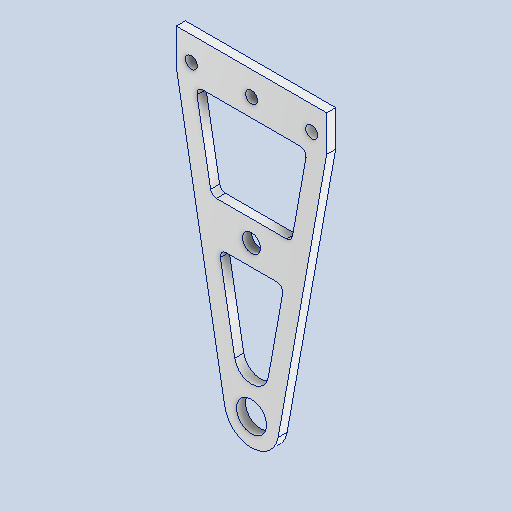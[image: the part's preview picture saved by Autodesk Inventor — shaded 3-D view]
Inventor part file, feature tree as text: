
AUTODESK INVENTOR PART (.ipt)
format: ipt  version: 2025.1 (Build 291241000, 241)  size: 143,360 bytes
history: native  units: mm
features: sketch x6, other x3
ambient origin geometry x8: Origin, YZ Plane, XZ Plane, XY Plane, X Axis, Y Axis, Z Axis, Center Point
bodies: Volumenkörper1 (feature_tree)
feature tree (9):
  other  "1171.ipt"
  other  "Volumenkörper1::1171.ipt"
  other  "TaggingFeature1"
  sketch  "Skizze1"  dims[d0=10.0mm]
  sketch  "Skizze3"
  sketch  "Skizze4"
  sketch  "Skizze5"
  sketch  "Skizze6"
  sketch  "Skizze7"
